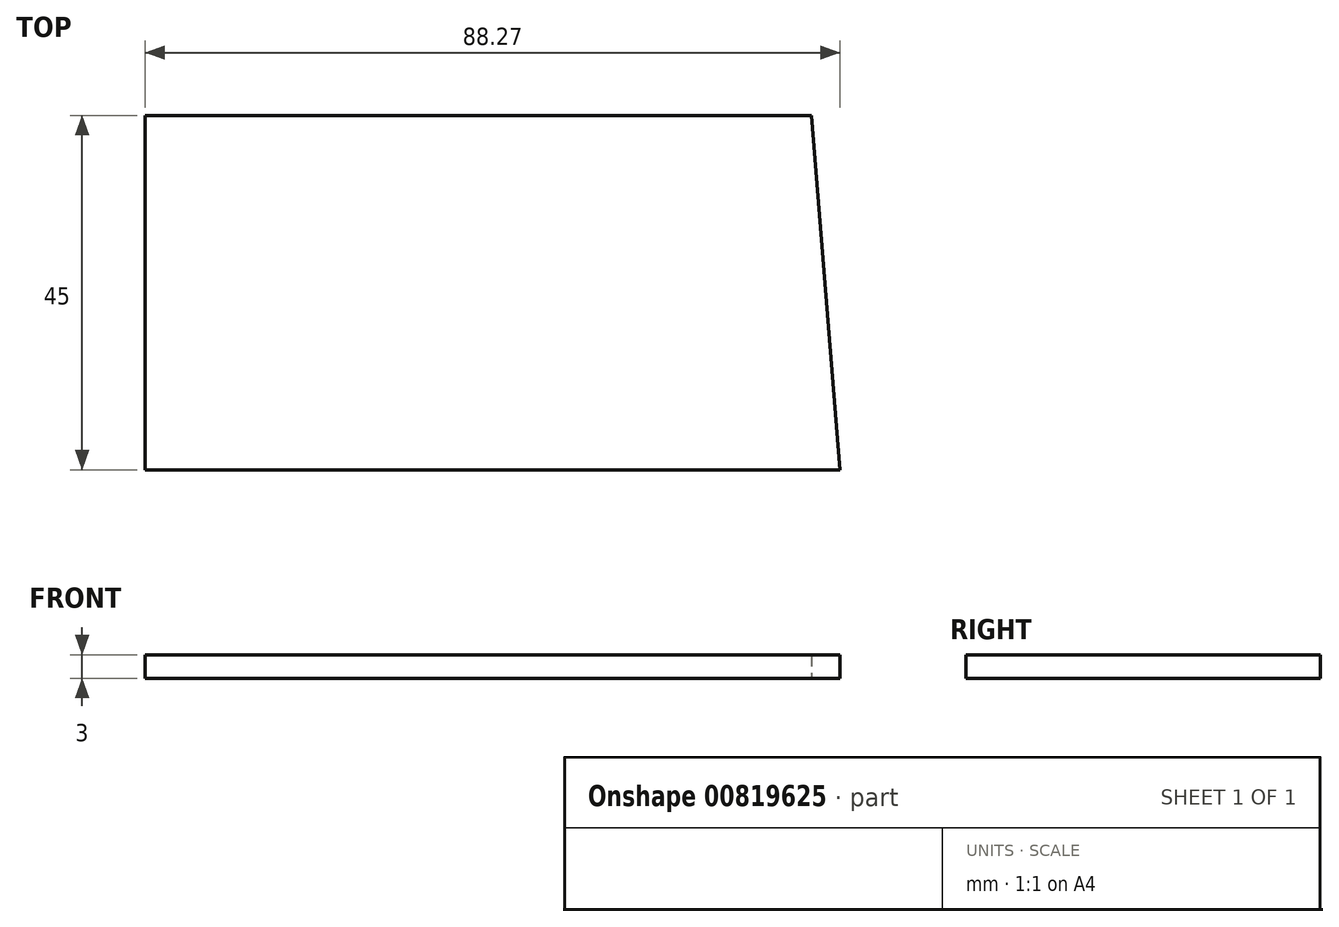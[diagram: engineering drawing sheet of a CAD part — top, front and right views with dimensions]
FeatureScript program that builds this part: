
annotation { "Feature Type Name" : "Feature", "Feature Type Description" : "" }
export const myFeature = defineFeature(function(context is Context, id is Id, definition is map)
    precondition{}
    {
        {
            var Q0;
            Q0=qCreatedBy(makeId("Top.planeOp"),FACE);
            var sketch = newSketch(context, id + "F0", { "sketchPlane" : qUnion([Q0])});
            skLineSegment(sketch, "E0", {"start": v(84.65, 0) * mm, "end": v(0, 0) * mm});
            skLineSegment(sketch, "E1", {"start": v(0, 0) * mm, "end": v(0, -45) * mm});
            skLineSegment(sketch, "E2", {"start": v(0, -45) * mm, "end": v(88.27, -45) * mm});
            skLineSegment(sketch, "E3", {"start": v(88.27, -45) * mm, "end": v(84.65, 0) * mm});
            skSolve(sketch);
        }
        {
            var Q0;
            Q0=makeQuery(id+"F0.imprint","IMPRINT",FACE,{"disambiguationData":[TD([[makeQuery(id+"F0.imprint","IMPRINT",EDGE,{"derivedFrom":sQuery(id+"F0.wireOp",EDGE,"E0")}),1.0]])]});
            var sketch = newSketch(context, id + "F1", { "sketchPlane" : qUnion([Q0])});
            skSolve(sketch);
        }
        {
            var Q0;
            Q0 = qSketchRegion(id + "F0", true);
            var Q1;
            Q1=makeQuery(id+"F1.imprint","IMPRINT",FACE,{"disambiguationData":[TD([[makeQuery(id+"F1.imprint","IMPRINT",EDGE,{"derivedFrom":makeQuery(id+"F0.imprint","IMPRINT",EDGE,{"derivedFrom":sQuery(id+"F0.wireOp",EDGE,"E0")})}),1.0]])]});
            extrude(context, id + "F2", {"entities" : qUnion([Q0, Q1]), "depth" : 3 * mm, "offsetDistance" : 25.4 * mm});
        }
    });
